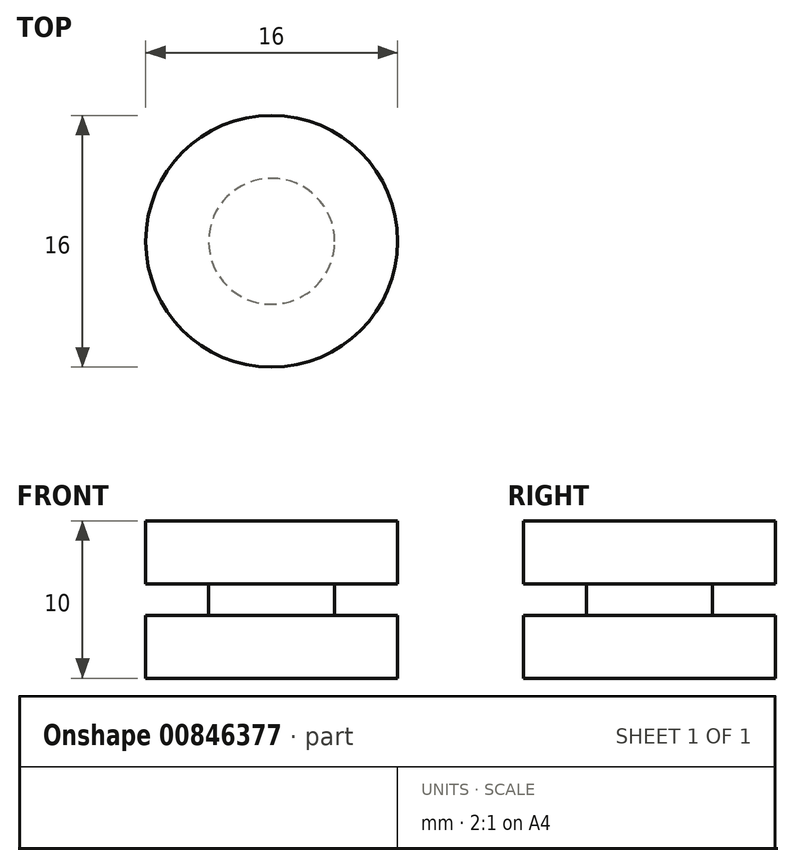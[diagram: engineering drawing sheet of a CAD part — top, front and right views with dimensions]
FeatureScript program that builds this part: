
annotation { "Feature Type Name" : "Feature", "Feature Type Description" : "" }
export const myFeature = defineFeature(function(context is Context, id is Id, definition is map)
    precondition{}
    {
        {
            var Q0;
            Q0=qCreatedBy(makeId("Front.planeOp"),FACE);
            var sketch = newSketch(context, id + "F0", { "sketchPlane" : qUnion([Q0])});
            skLineSegment(sketch, "E0", {"start": v(0, 0) * mm, "end": v(0, 50) * mm, "construction": true});
            skLineSegment(sketch, "E1", {"start": v(0, 0) * mm, "end": v(8, 0) * mm});
            skLineSegment(sketch, "E2", {"start": v(8, 0) * mm, "end": v(8, 4) * mm});
            skLineSegment(sketch, "E3", {"start": v(8, 4) * mm, "end": v(4, 4) * mm});
            skLineSegment(sketch, "E4", {"start": v(4, 4) * mm, "end": v(4, 6) * mm});
            skLineSegment(sketch, "E5", {"start": v(4, 6) * mm, "end": v(8, 6) * mm});
            skLineSegment(sketch, "E6", {"start": v(8, 6) * mm, "end": v(8, 10) * mm});
            skLineSegment(sketch, "E7", {"start": v(8, 10) * mm, "end": v(0, 10) * mm});
            skLineSegment(sketch, "E8", {"start": v(0, 10) * mm, "end": v(0, 0) * mm});
            skSolve(sketch);
        }
        {
            var Q0;
            Q0 = qSketchRegion(id + "F0", true);
            var Q1;
            Q1=sQuery(id+"F0.wireOp",EDGE,"E0");
            revolve(context, id + "F1", {"surfaceOperationType" : NewSurfaceOperationType.NEW, "entities" : qUnion([Q0]), "axis" : qUnion([Q1]), "revolveType" : RevolveType.FULL});
        }
    });
